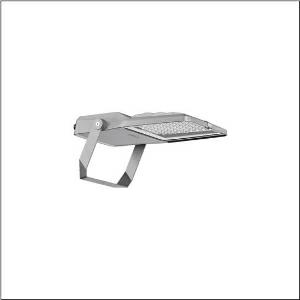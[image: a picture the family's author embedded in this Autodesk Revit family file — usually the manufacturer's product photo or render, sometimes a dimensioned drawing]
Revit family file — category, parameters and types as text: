
# Revit family: floodlight_fl_21_iq_mini___pl43_5xa7772d4a1a_cd74
name_source: partatom
category: Lighting Fixtures
units: mm (PartAtom-declared; Revit-internal decimal feet)

## family parameters
Cut with Voids When Loaded = No
Host = Face
Light Source = No
Part Type = Normal
Room Calculation Point = No
Round Connector Dimension = Use Diameter
Shared = No

## types (1)
- --- (1 x LED, 19090 lm, 143 W, 4000K)
    Apparent Load = 143 VA
    CIE Flux Codes = 27 78 99 100 100
    Color Rendering = 70
    Color Temperature = 4000K
    Default Elevation = 1800 mm
    Description = Floodlight FL 21 iQ mini, floodlight, primary light control with lens, of PMMA, primary optical cover: protective disc, of toughened safety glass, transparent, light distribution: PL43, light emission: direct distribution, installation type: surface-mounted, lamps: LED, High Power LED, rated values: 19.090lm | 143W | 133,5lm/W (begin service life); end service life: 19.090lm | 151,6W; at 50% lumin. flux: 9.545lm | 60,8W | 157lm/W, colour temperature: 4000K, colour rendering: CRI > 70, light colour: 740, light setting 1 begin service life: 100% | 19.090lm | 143W | 133,5lm/W | 4.000K, light setting 1 end service life: 151,6W, further light settings possible, control: Street-Remote, Auto-Match, Temp-Guard, Night-Set, Smart-Wire, Desk-Remote (wireless, voltage-free reading and setting of iQ features in the workshop via application-optimized NFC function/RFID function), optimised constant luminous flux control (CLO 2.0), pre-setting: linear dimming characteristic, with terminal, 6-pole, mains connection: 220..240V, AC, 50/60Hz, luminaire housing, of diecast aluminium, powder-coated, SITECO metallic grey (DB 702S), corrosivity category C5 mid according to DIN EN ISO 12944suitable for swimming poolschlorine-resistant, sealing non-destructively replaceable, mounting bracket, of steel, galvanised, powder-coated, SITECO metallic grey (DB 702S), protection rating (complete): IP66, insulation class (complete): insulation class II (safety insulation), certification: CE, ENEC, VDE, protection symbol: D, impact resistance: IK08, permissible operating ambient temperature: -40..+40°C, permissible operating ambient temperature for outdoor applications: -40..+50°C, standard: DIN EN 12944, LABS conformity tested according to VDMA 24364:2018-05, packaging unit: 1 piece

Light Distribution: PL43
    Height = 70 mm
    Lamp = 1 x LED
    Lamp Light Flux = 19090 lm
    Lamp Power = 143 W
    Lamp count = 1
    Length = 485 mm
    Luminous efficacy = 133 lm/W
    Manufacturer = Siteco
    ModVariant = No
    Model = 5XA7772D4A1A
    Number of Poles = 1
    OnlyDefault = Yes
    Power Factor = 1
    Product Name = Floodlight FL 21 iQ mini | PL43
    Product group = floodlight | pylon annexe
    ProductGroupID = 6201
    Protection Class = Protection class II
    Protection Degree = IP 66
    RLX_Detail_Level = 1
    RLX_Emergency_Light_Flux = 0 lm
    RLX_Emergency_Type = 0
    RLX_Emergency_Type_DB = No
    RlxData = <blob elided: 96653 chars, md5=1e6ce33b>
    Socket = socket
    Standby Power = 0 W
    System Light Flux = 19090 lm
    System Power = 143 W
    Type Comments = factory setting: luminous flux: 100 % | dim-lin: 254 | 730 mA
    Type Image = l_1006845.jpg
    URL = http://relux.com
    VarID = @adj_160821
    Voltage = 0 V
    Weight = 0.00 kg
    Width = 337 mm

## geometry (parser evidence)
native form markers: Blend x4, Sweep x13
no freeform markers — native parametric forms only
